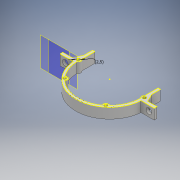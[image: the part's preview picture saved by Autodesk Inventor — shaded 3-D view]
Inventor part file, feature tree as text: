
AUTODESK INVENTOR PART (.ipt)
format: ipt  version: 2017 (Build 210142000, 142)  size: 192,000 bytes
history: native  units: mm
features: sketch x3, projected_geometry x3, other x2, extrude x2
ambient origin geometry x8: Origin, YZ Plane, XZ Plane, XY Plane, X Axis, Y Axis, Z Axis, Center Point
bodies: Body1 (feature_tree)
feature tree (10):
  sketch  "Esquisse1"
  other  "Plan de construction1"
  other  "Plan de construction2"
  sketch  "Esquisse3"
  extrude  "Extrusion14"  Depth=2.0mm
  extrude  "Extrusion15"  Depth=2.0mm
  sketch  "Esquisse4"
  projected_geometry  "Boucle projetée3"
  projected_geometry  "Boucle projetée4"
  projected_geometry  "Boucle projetée5"
